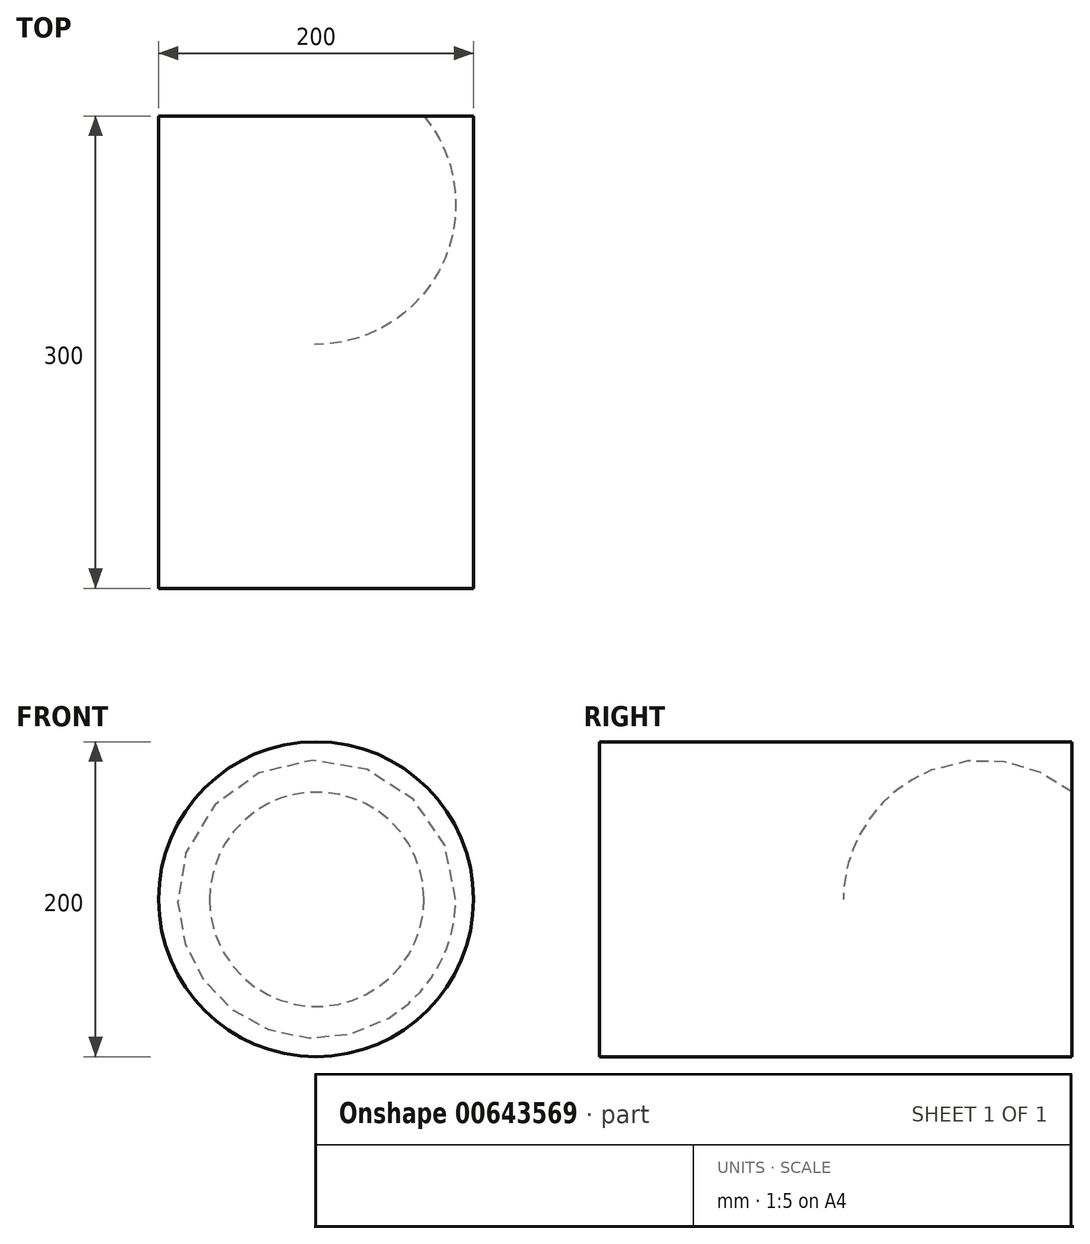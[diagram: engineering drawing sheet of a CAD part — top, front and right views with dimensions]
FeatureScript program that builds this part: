
annotation { "Feature Type Name" : "Feature", "Feature Type Description" : "" }
export const myFeature = defineFeature(function(context is Context, id is Id, definition is map)
    precondition{}
    {
        {
            var Q0;
            Q0=qCreatedBy(makeId("Front.planeOp"),FACE);
            var sketch = newSketch(context, id + "F0", { "sketchPlane" : qUnion([Q0])});
            skCircle(sketch, "E0", {"center": v(0, 0) * mm, "radius": 100 * mm});
            skSolve(sketch);
        }
        {
            var Q0;
            Q0 = qSketchRegion(id + "F0", true);
            extrude(context, id + "F1", {"entities" : qUnion([Q0]), "depth" : 300 * mm, "offsetDistance" : 25 * mm});
        }
        {
            var Q0;
            Q0=qCreatedBy(makeId("Top.planeOp"),FACE);
            var sketch = newSketch(context, id + "F2", { "sketchPlane" : qUnion([Q0])});
            skArc(sketch, "E1", {"start": v(0.93, 32.43) * mm, "mid": v(-87.82, -55.85) * mm, "end": v(0, -145.06) * mm});
            skLineSegment(sketch, "E2", {"start": v(0, -145.06) * mm, "end": v(0.93, 32.43) * mm});
            skSolve(sketch);
        }
        {
            var Q0;
            Q0=makeQuery(id+"F2.imprint","IMPRINT",FACE,{"disambiguationData":[TD([[makeQuery(id+"F2.imprint","IMPRINT",EDGE,{"derivedFrom":sQuery(id+"F2.wireOp",EDGE,"E1")}),1.0]])]});
            var Q1;
            Q1=sQuery(id+"F2.wireOp",EDGE,"E2");
            revolve(context, id + "F3", {"operationType" : NewBodyOperationType.REMOVE, "entities" : qUnion([Q0]), "axis" : qUnion([Q1]), "revolveType" : RevolveType.FULL, "oppositeDirection" : true});
        }
    });
